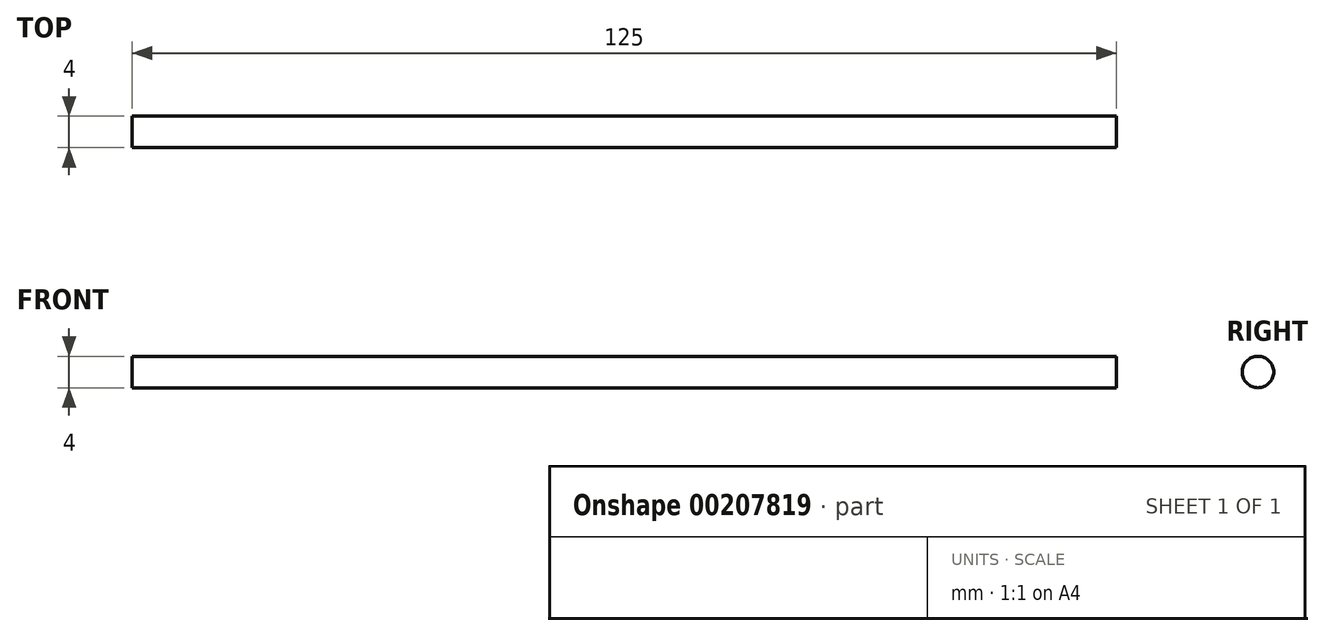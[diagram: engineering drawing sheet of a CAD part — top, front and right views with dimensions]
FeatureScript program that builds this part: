
annotation { "Feature Type Name" : "Feature", "Feature Type Description" : "" }
export const myFeature = defineFeature(function(context is Context, id is Id, definition is map)
    precondition{}
    {
        {
            var Q0;
            Q0=qCreatedBy(makeId("Right.planeOp"),FACE);
            var sketch = newSketch(context, id + "F0", { "sketchPlane" : qUnion([Q0])});
            skCircle(sketch, "E0", {"center": v(0, 0) * mm, "radius": 2 * mm});
            skSolve(sketch);
        }
        {
            var Q0;
            Q0 = qSketchRegion(id + "F0", true);
            extrude(context, id + "F1", {"entities" : qUnion([Q0]), "endBound" : BoundingType.SYMMETRIC, "depth" : 125 * mm});
        }
    });
